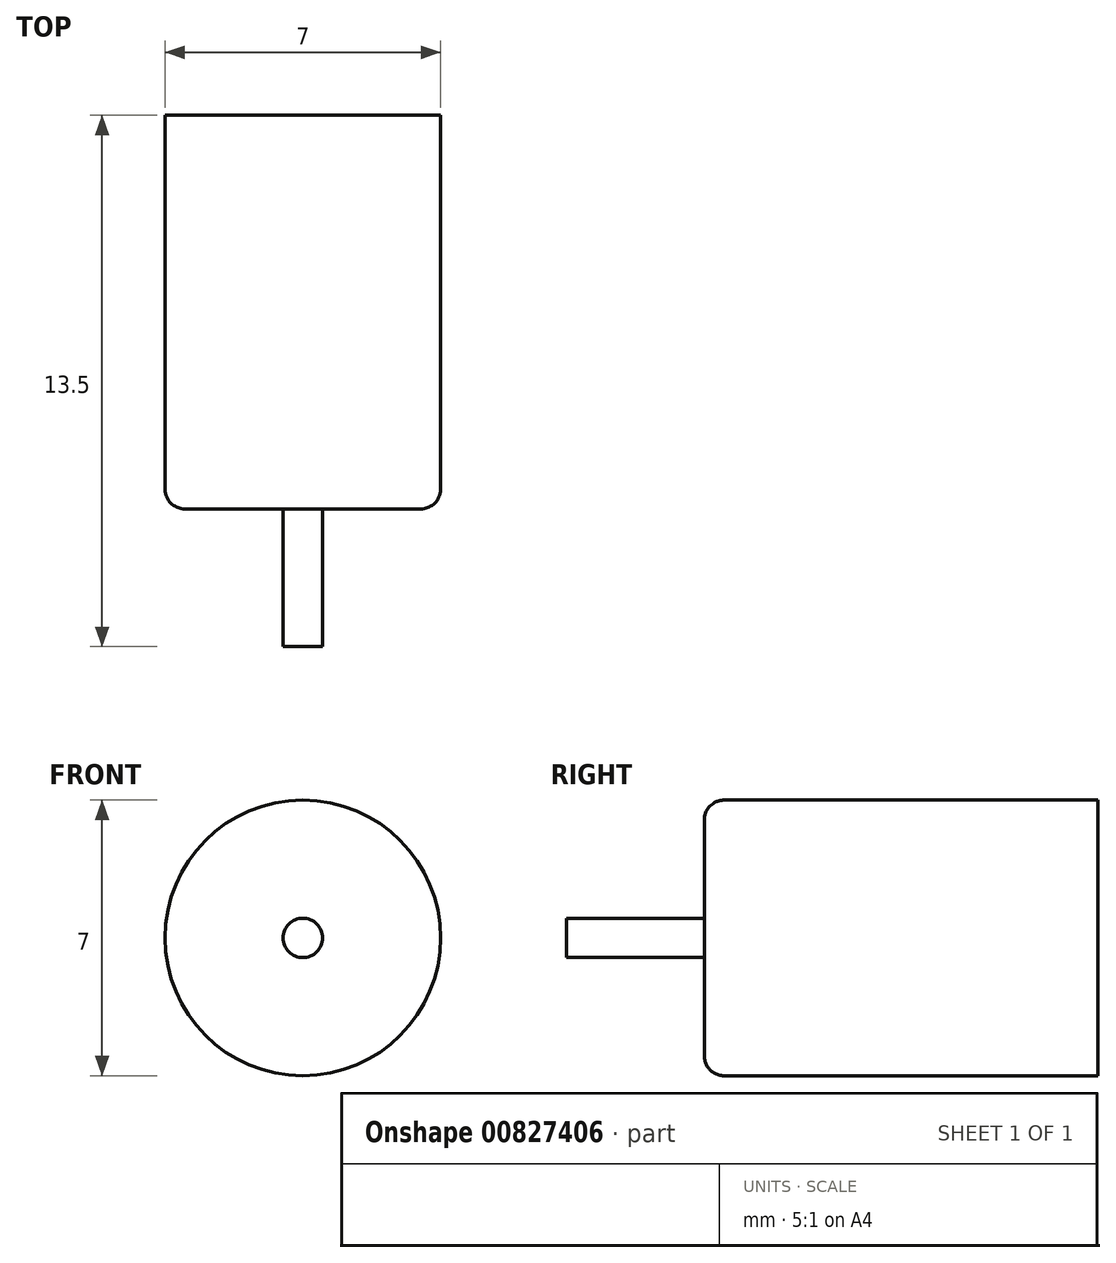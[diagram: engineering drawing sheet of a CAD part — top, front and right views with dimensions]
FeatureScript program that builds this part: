
annotation { "Feature Type Name" : "Feature", "Feature Type Description" : "" }
export const myFeature = defineFeature(function(context is Context, id is Id, definition is map)
    precondition{}
    {
        {
            var Q0;
            Q0=qCreatedBy(makeId("Front.planeOp"),FACE);
            var sketch = newSketch(context, id + "F0", { "sketchPlane" : qUnion([Q0])});
            skCircle(sketch, "E0", {"center": v(0, 0) * mm, "radius": 3.5 * mm});
            skSolve(sketch);
        }
        {
            var Q0;
            Q0=makeQuery(id+"F0.imprint","IMPRINT",FACE,{"disambiguationData":[TD([[makeQuery(id+"F0.imprint","IMPRINT",EDGE,{"derivedFrom":sQuery(id+"F0.wireOp",EDGE,"E0")}),1.0]])]});
            extrude(context, id + "F1", {"entities" : qUnion([Q0]), "depth" : 10 * mm, "offsetDistance" : 25 * mm});
        }
        {
            var Q0;
            Q0=makeQuery(id+"F1.opExtrude","CAP_EDGE",EDGE,{"disambiguationData":[OSD([sQuery(id+"F0.wireOp",EDGE,"E0")])],"isStart":false});
            fillet(context, id + "F2", {"entities" : qUnion([Q0]), "radius" : 0.5 * mm, "tangentPropagation" : true, "allowEdgeOverflow" : false});
        }
        {
            var Q0;
            Q0=makeQuery(id+"F1.opExtrude","CAP_FACE",FACE,{"disambiguationData":[OSD([sQuery(id+"F0.wireOp",EDGE,"E0")])],"isStart":false});
            var sketch = newSketch(context, id + "F3", { "sketchPlane" : qUnion([Q0])});
            skCircle(sketch, "E1", {"center": v(0, 0) * mm, "radius": 0.5 * mm});
            skSolve(sketch);
        }
        {
            var Q0;
            Q0=makeQuery(id+"F3.imprint","IMPRINT",FACE,{"disambiguationData":[TD([[makeQuery(id+"F3.imprint","IMPRINT",EDGE,{"derivedFrom":sQuery(id+"F3.wireOp",EDGE,"E1")}),1.0]])]});
            extrude(context, id + "F4", {"entities" : qUnion([Q0]), "operationType" : NewBodyOperationType.ADD, "depth" : 3.5 * mm, "offsetDistance" : 25 * mm});
        }
    });
